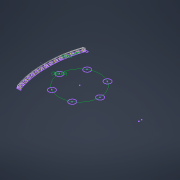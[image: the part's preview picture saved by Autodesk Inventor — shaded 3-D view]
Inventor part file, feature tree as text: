
AUTODESK INVENTOR PART (.ipt)
format: ipt  version: 2022 (Build 260153000, 153)  size: 202,752 bytes
history: native  units: mm
features: sketch x3, fillet x2, extrude x1, hole x1
ambient origin geometry x8: Origin, YZ Plane, XZ Plane, XY Plane, X Axis, Y Axis, Z Axis, Center Point
bodies: Solid1 (feature_tree)
feature tree (7):
  sketch  "Sketch2"  dims[d1=60.0mm d5=360.0deg d24=4.5mm d25=0.0mm d26=2.498mm]
  extrude  "Extrusion1"  Depth=2.498mm TaperAngle=0.0deg
  fillet  "Fillet1"  Radius=2.498mm
  sketch  "Sketch3"  dims[d28=8.061767mm]
  sketch  "Sketch5"  dims[d31=4.8mm d32=6.0mm d33=4.0mm d34=2.0mm d35=90.0deg d36=2.5mm d37=0.0mm d38=2.4mm d39=1.0mm d40=1.0mm d41=1.0mm d42=0.15mm d43=0.25mm d44=0.375mm d45=14.3117mm d46=0.75mm d47=20.594885mm d48=0.0625mm d49=0.75mm d50=0.375mm]
  hole  "Hole1"  [1 undecoded]
  fillet  "Fillet2"  Radius=1.0mm
note: 1 required parameter value undecoded (feature->parameter linkage not recoverable at this tier; creation-order binding heuristic only, values carry confidence <= 0.55)
